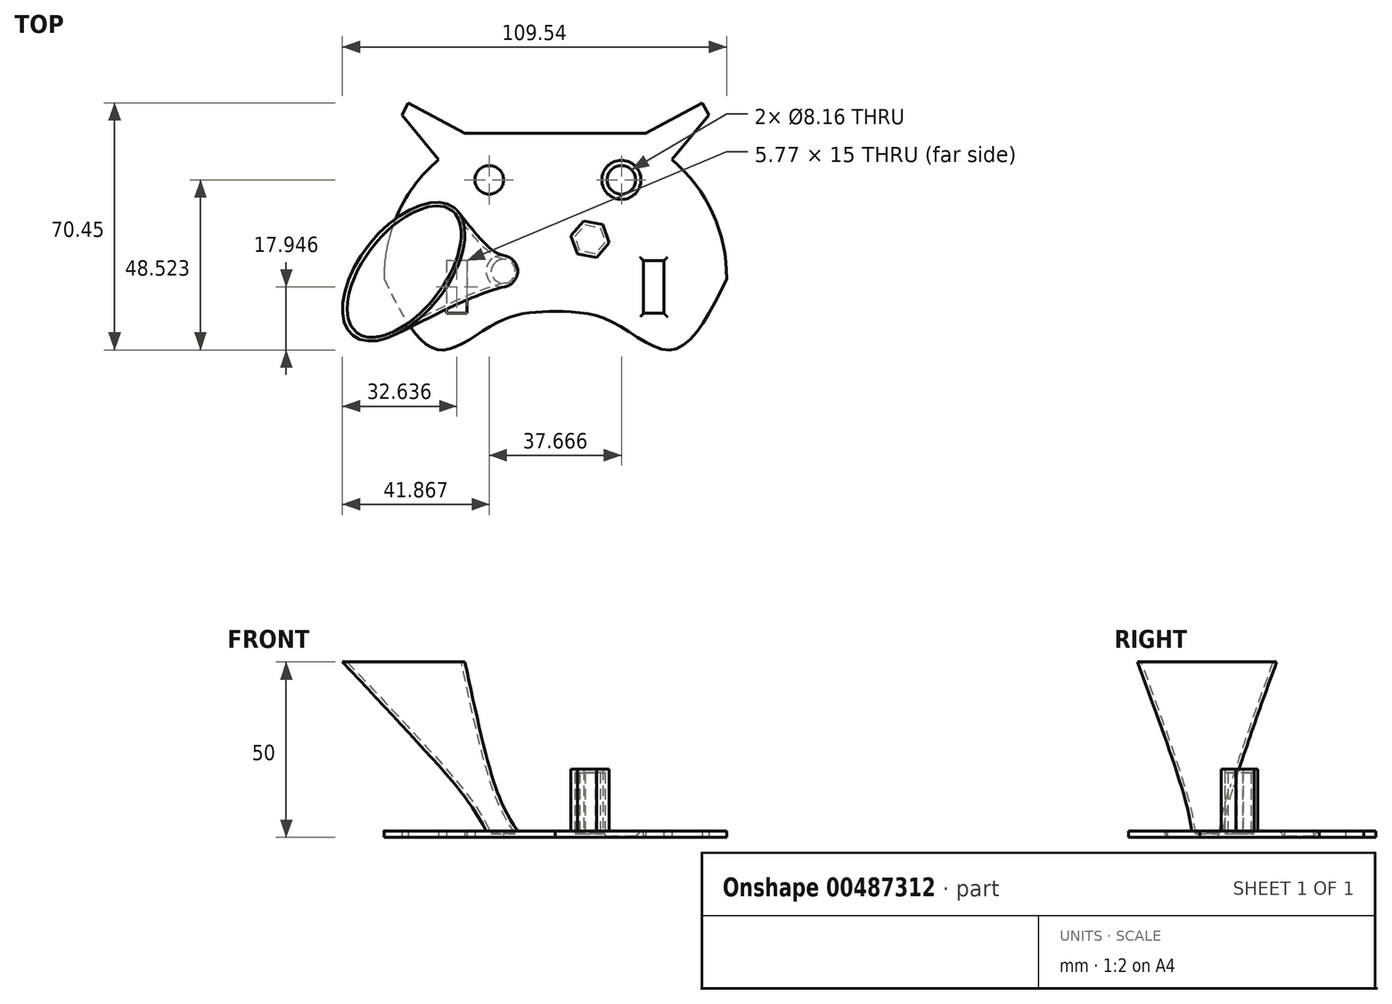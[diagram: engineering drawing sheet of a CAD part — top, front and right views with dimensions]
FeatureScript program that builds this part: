
annotation { "Feature Type Name" : "Feature", "Feature Type Description" : "" }
export const myFeature = defineFeature(function(context is Context, id is Id, definition is map)
    precondition{}
    {
        {
            var Q0;
            Q0=qCreatedBy(makeId("Top.planeOp"),FACE);
            var sketch = newSketch(context, id + "F0", { "sketchPlane" : qUnion([Q0])});
            skLineSegment(sketch, "E0", {"start": v(0, 31.26) * mm, "end": v(25.76, 31.26) * mm});
            skLineSegment(sketch, "E1", {"start": v(25.76, 31.26) * mm, "end": v(41.91, 39.92) * mm});
            skLineSegment(sketch, "E2", {"start": v(41.91, 39.92) * mm, "end": v(43.74, 36.5) * mm});
            skLineSegment(sketch, "E3", {"start": v(43.74, 36.5) * mm, "end": v(33.26, 23.76) * mm});
            skArc(sketch, "E4", {"start": v(48.83, -10.28) * mm, "mid": v(44.85, 8.49) * mm, "end": v(33.26, 23.76) * mm});
            skFitSpline(sketch, "E5", {"points": [v(48.83, -10.28) * mm, v(33.26, -30.47) * mm, v(15.95, -22.4) * mm, v(0, -19.5) * mm], "startDerivative": vector(-38.12, -77.32) * mm, "endDerivative": vector(-52.58, 1.1) * mm});
            skCircle(sketch, "E6", {"center": v(18.83, 18) * mm, "radius": 4.08 * mm});
            skLineSegment(sketch, "E7.bottom", {"start": v(25.18, -5.08) * mm, "end": v(30.95, -5.08) * mm});
            skLineSegment(sketch, "E7.top", {"start": v(25.18, -20.08) * mm, "end": v(30.95, -20.08) * mm});
            skLineSegment(sketch, "E7.left", {"start": v(25.18, -5.08) * mm, "end": v(25.18, -20.08) * mm});
            skLineSegment(sketch, "E7.right", {"start": v(30.95, -5.08) * mm, "end": v(30.95, -20.08) * mm});
            skLineSegment(sketch, "E8", {"start": v(0, 47.45) * mm, "end": v(0, -33.7) * mm, "construction": true});
            skLineSegment(sketch, "E9.MirrorCS", {"start": v(-41.91, 39.92) * mm, "end": v(-43.74, 36.5) * mm});
            skLineSegment(sketch, "E10.MirrorCS", {"start": v(-25.18, -5.08) * mm, "end": v(-30.95, -5.08) * mm});
            skLineSegment(sketch, "E11.MirrorCS", {"start": v(-25.18, -20.08) * mm, "end": v(-30.95, -20.08) * mm});
            skLineSegment(sketch, "E12.MirrorCS", {"start": v(0, 31.26) * mm, "end": v(-25.76, 31.26) * mm});
            skLineSegment(sketch, "E13.MirrorCS", {"start": v(-25.76, 31.26) * mm, "end": v(-41.91, 39.92) * mm});
            skLineSegment(sketch, "E14.MirrorCS", {"start": v(-43.74, 36.5) * mm, "end": v(-33.26, 23.76) * mm});
            skArc(sketch, "E15.MirrorCS", {"start": v(-48.83, -10.28) * mm, "mid": v(-44.85, 8.49) * mm, "end": v(-33.26, 23.76) * mm});
            skFitSpline(sketch, "E16.MirrorCS", {"points": [v(-48.83, -10.28) * mm, v(-33.26, -30.47) * mm, v(-15.95, -22.4) * mm, v(0, -19.5) * mm], "startDerivative": vector(38.12, -77.32) * mm, "endDerivative": vector(52.58, 1.1) * mm});
            skCircle(sketch, "E17.MirrorC", {"center": v(-18.83, 18) * mm, "radius": 4.08 * mm});
            skLineSegment(sketch, "E18.MirrorCS", {"start": v(-25.18, -5.08) * mm, "end": v(-25.18, -20.08) * mm});
            skLineSegment(sketch, "E19.MirrorCS", {"start": v(-30.95, -5.08) * mm, "end": v(-30.95, -20.08) * mm});
            skSolve(sketch);
        }
        {
            var Q0;
            Q0=makeQuery(id+"F0.imprint","IMPRINT",FACE,{"disambiguationData":[TD([[makeQuery(id+"F0.imprint","IMPRINT",EDGE,{"derivedFrom":sQuery(id+"F0.wireOp",EDGE,"E0")}),-1.0]])]});
            extrude(context, id + "F1", {"entities" : qUnion([Q0]), "depth" : 1.8 * mm});
        }
        {
            var Q0;
            Q0=makeQuery(id+"F1.opExtrude","CAP_EDGE",EDGE,{"disambiguationData":[OSD([sQuery(id+"F0.wireOp",EDGE,"E7.left")])],"isStart":false});
            var Q1;
            Q1=makeQuery(id+"F1.opExtrude","CAP_EDGE",EDGE,{"disambiguationData":[OSD([sQuery(id+"F0.wireOp",EDGE,"E7.bottom")])],"isStart":false});
            var Q2;
            Q2=makeQuery(id+"F1.opExtrude","CAP_EDGE",EDGE,{"disambiguationData":[OSD([sQuery(id+"F0.wireOp",EDGE,"E7.right")])],"isStart":false});
            var Q3;
            Q3=makeQuery(id+"F1.opExtrude","CAP_EDGE",EDGE,{"disambiguationData":[OSD([sQuery(id+"F0.wireOp",EDGE,"E7.top")])],"isStart":false});
            fillet(context, id + "F2", {"entities" : qUnion([Q0, Q1, Q2, Q3]), "radius" : 1 * mm, "tangentPropagation" : true, "allowEdgeOverflow" : false});
        }
        {
            var Q0;
            Q0=makeQuery(id+"F1.opExtrude","CAP_EDGE",EDGE,{"disambiguationData":[OSD([sQuery(id+"F0.wireOp",EDGE,"E6")])],"isStart":false});
            chamfer(context, id + "F3", {"entities" : qUnion([Q0]), "width" : 1.5 * mm, "tangentPropagation" : true});
        }
        {
            var Q0;
            Q0=makeQuery(id+"F1.opExtrude","CAP_FACE",FACE,{"disambiguationData":[OSD([sQuery(id+"F0.wireOp",EDGE,"E0"),sQuery(id+"F0.wireOp",EDGE,"E1"),sQuery(id+"F0.wireOp",EDGE,"E2"),sQuery(id+"F0.wireOp",EDGE,"E3"),sQuery(id+"F0.wireOp",EDGE,"E4"),sQuery(id+"F0.wireOp",EDGE,"E5"),sQuery(id+"F0.wireOp",EDGE,"E6"),sQuery(id+"F0.wireOp",EDGE,"E7.bottom"),sQuery(id+"F0.wireOp",EDGE,"E7.top"),sQuery(id+"F0.wireOp",EDGE,"E7.left"),sQuery(id+"F0.wireOp",EDGE,"E7.right"),sQuery(id+"F0.wireOp",EDGE,"E9.MirrorCS"),sQuery(id+"F0.wireOp",EDGE,"E10.MirrorCS"),sQuery(id+"F0.wireOp",EDGE,"E11.MirrorCS"),sQuery(id+"F0.wireOp",EDGE,"E12.MirrorCS"),sQuery(id+"F0.wireOp",EDGE,"E13.MirrorCS"),sQuery(id+"F0.wireOp",EDGE,"E14.MirrorCS"),sQuery(id+"F0.wireOp",EDGE,"E15.MirrorCS"),sQuery(id+"F0.wireOp",EDGE,"E16.MirrorCS"),sQuery(id+"F0.wireOp",EDGE,"E17.MirrorC"),sQuery(id+"F0.wireOp",EDGE,"E18.MirrorCS"),sQuery(id+"F0.wireOp",EDGE,"E19.MirrorCS")])],"isStart":false});
            var sketch = newSketch(context, id + "F4", { "sketchPlane" : qUnion([Q0])});
            skCircle(sketch, "E20.cCircle", {"center": v(9.9, 1.04) * mm, "radius": 4.82 * mm, "construction": true});
            skLineSegment(sketch, "E20.0", {"start": v(8.08, 6.3) * mm, "end": v(13.54, 5.25) * mm});
            skLineSegment(sketch, "E20.1", {"start": v(13.54, 5.25) * mm, "end": v(15.36, 0) * mm});
            skLineSegment(sketch, "E20.2", {"start": v(15.36, 0) * mm, "end": v(11.72, -4.21) * mm});
            skLineSegment(sketch, "E20.3", {"start": v(11.72, -4.21) * mm, "end": v(6.26, -3.17) * mm});
            skLineSegment(sketch, "E20.4", {"start": v(6.26, -3.17) * mm, "end": v(4.44, 2.09) * mm});
            skLineSegment(sketch, "E20.5", {"start": v(4.44, 2.09) * mm, "end": v(8.08, 6.3) * mm});
            skPoint(sketch, "E20.0.midPoint", {"position": v(10.8, 5.77) * mm});
            skSolve(sketch);
        }
        {
            var Q0;
            Q0=makeQuery(id+"F4.imprint","IMPRINT",FACE,{"disambiguationData":[TD([[makeQuery(id+"F4.imprint","IMPRINT",EDGE,{"derivedFrom":sQuery(id+"F4.wireOp",EDGE,"E20.0")}),-1.0]])]});
            extrude(context, id + "F5", {"entities" : qUnion([Q0]), "operationType" : NewBodyOperationType.ADD, "depth" : 17.6 * mm});
        }
        {
            var Q0;
            Q0=makeQuery(id+"F1.opExtrude","CAP_FACE",FACE,{"disambiguationData":[OSD([sQuery(id+"F0.wireOp",EDGE,"E0"),sQuery(id+"F0.wireOp",EDGE,"E1"),sQuery(id+"F0.wireOp",EDGE,"E2"),sQuery(id+"F0.wireOp",EDGE,"E3"),sQuery(id+"F0.wireOp",EDGE,"E4"),sQuery(id+"F0.wireOp",EDGE,"E5"),sQuery(id+"F0.wireOp",EDGE,"E6"),sQuery(id+"F0.wireOp",EDGE,"E7.bottom"),sQuery(id+"F0.wireOp",EDGE,"E7.top"),sQuery(id+"F0.wireOp",EDGE,"E7.left"),sQuery(id+"F0.wireOp",EDGE,"E7.right"),sQuery(id+"F0.wireOp",EDGE,"E9.MirrorCS"),sQuery(id+"F0.wireOp",EDGE,"E10.MirrorCS"),sQuery(id+"F0.wireOp",EDGE,"E11.MirrorCS"),sQuery(id+"F0.wireOp",EDGE,"E12.MirrorCS"),sQuery(id+"F0.wireOp",EDGE,"E13.MirrorCS"),sQuery(id+"F0.wireOp",EDGE,"E14.MirrorCS"),sQuery(id+"F0.wireOp",EDGE,"E15.MirrorCS"),sQuery(id+"F0.wireOp",EDGE,"E16.MirrorCS"),sQuery(id+"F0.wireOp",EDGE,"E17.MirrorC"),sQuery(id+"F0.wireOp",EDGE,"E18.MirrorCS"),sQuery(id+"F0.wireOp",EDGE,"E19.MirrorCS")])],"isStart":false});
            var sketch = newSketch(context, id + "F6", { "sketchPlane" : qUnion([Q0])});
            skCircle(sketch, "E21", {"center": v(-15.24, -8.07) * mm, "radius": 4.5 * mm});
            skSolve(sketch);
        }
        {
            var Q0;
            Q0=qCreatedBy(makeId("Top.planeOp"),FACE);
            cPlane(context, id + "F7", {"entities" : qUnion([Q0]), "cplaneType" : CPlaneType.OFFSET, "offset" : 50 * mm, "width" : 150 * mm, "height" : 150 * mm});
        }
        {
            var Q0;
            Q0=qCreatedBy(id+"F7.planeOp",FACE);
            var sketch = newSketch(context, id + "F8", { "sketchPlane" : qUnion([Q0])});
            skEllipse(sketch, "E22", {"center": v(-43.24, -8.2) * mm, "majorRadius": 23.24 * mm, "minorRadius": 12.53 * mm, "majorAxis": v(0.62, 0.78)});
            skSolve(sketch);
        }
        {
            var Q1;
            Q1=makeQuery(id+"F8.imprint","IMPRINT",FACE,{"disambiguationData":[TD([[makeQuery(id+"F8.imprint","IMPRINT",EDGE,{"derivedFrom":sQuery(id+"F8.wireOp",EDGE,"E22")}),1.0]])]});
            var Q2;
            Q2=makeQuery(id+"F6.imprint","IMPRINT",FACE,{"disambiguationData":[TD([[makeQuery(id+"F6.imprint","IMPRINT",EDGE,{"derivedFrom":sQuery(id+"F6.wireOp",EDGE,"E21")}),1.0]])]});
            var Q3;
            Q3=sQuery(id+"F6.wireOp",EDGE,"E21");
            var Q4;
            Q4=sQuery(id+"F8.wireOp",EDGE,"E22");
            loft(context, id + "F9", {"operationType" : NewBodyOperationType.ADD, "sheetProfilesArray" : [{ "sheetProfileEntities" : qUnion([Q1]) }, { "sheetProfileEntities" : qUnion([Q2]) }], "wireProfilesArray" : [{ "wireProfileEntities" : qUnion([Q3]) }, { "wireProfileEntities" : qUnion([Q4]) }]});
        }
        {
            var Q0;
            Q0=makeQuery(id+"F9.opLoft","CAP_FACE",FACE,{"disambiguationData":[OSD([makeQuery(id+"F8.imprint","IMPRINT",FACE,{"disambiguationData":[TD([[makeQuery(id+"F8.imprint","IMPRINT",EDGE,{"derivedFrom":sQuery(id+"F8.wireOp",EDGE,"E22")}),1.0]])]})])],"isStart":true});
            shell(context, id + "F10", {"entities" : qUnion([Q0]), "thickness" : 1 * mm});
        }
    });
